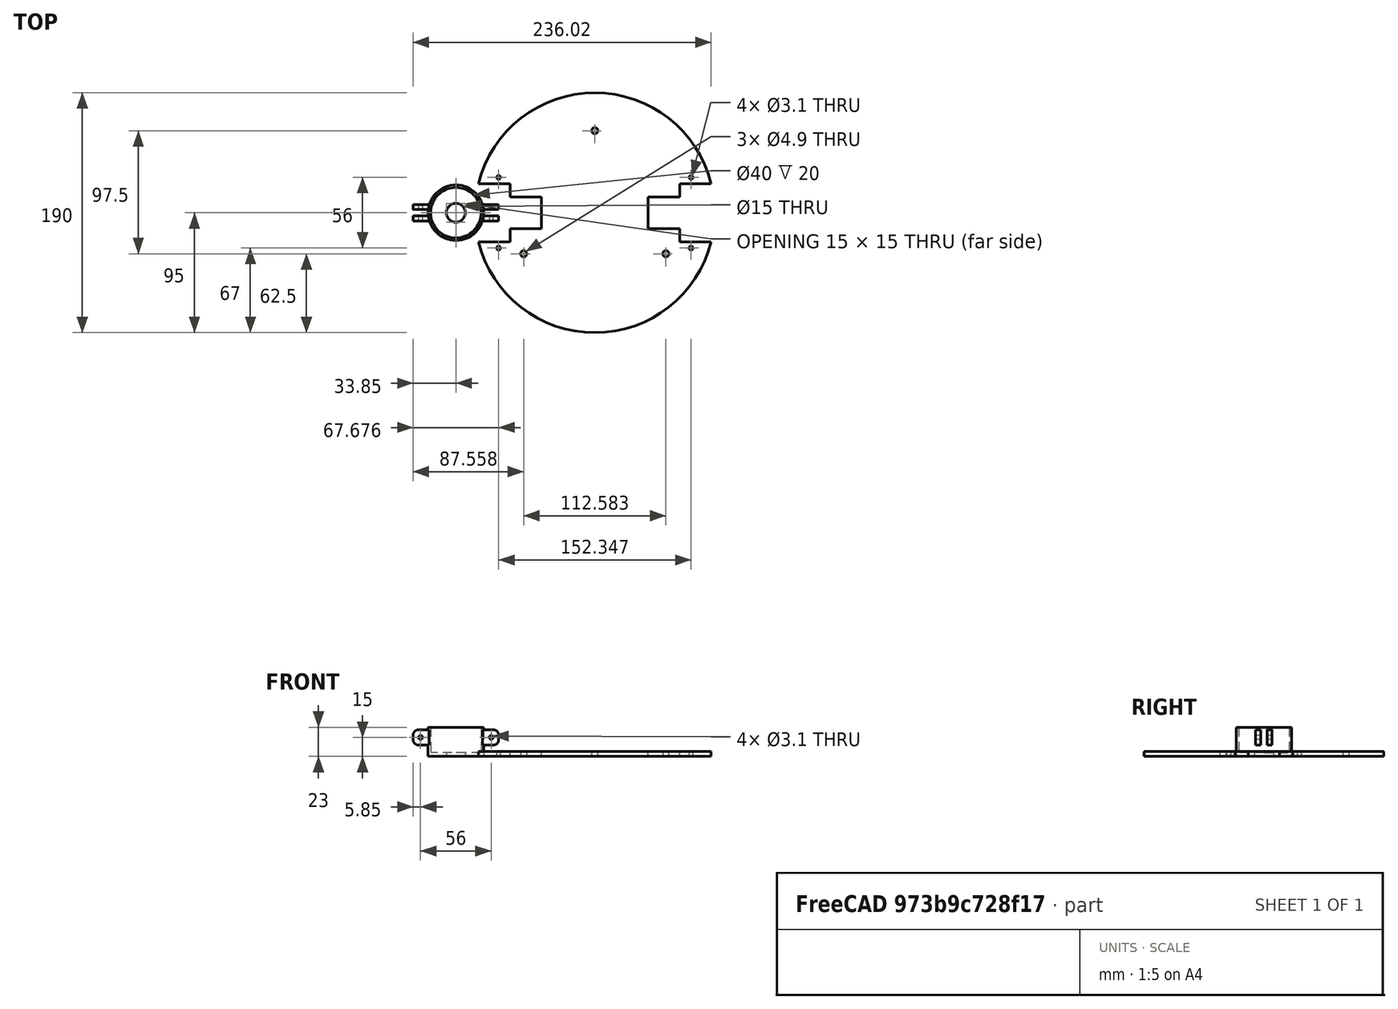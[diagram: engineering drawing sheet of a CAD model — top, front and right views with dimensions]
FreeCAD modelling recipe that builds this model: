
FCSTD DOCUMENT  (FreeCAD 1.0R39319 (Git))
Label: GyroBot
License: All rights reserved
LicenseURL: https://en.wikipedia.org/wiki/All_rights_reserved
objects: Sketcher::SketchObject×6, PartDesign::CoordinateSystem×5, PartDesign::Pad×4, App::DocumentObjectGroup×3, App::Link×3, PartDesign::Mirrored×2, PartDesign::Fillet×2, PartDesign::Body×2, PartDesign::Plane×1, PartDesign::Pocket×1, App::FeaturePython×1, App::Part×1, Mesh::Feature×1
note: 45 computed .brp shape members not serialized (recipe doc carries the construction recipe); baked Part::Feature solids carry a one-line shape summary decoded from their .brp

FEATURE [Sketcher::SketchObject] Sketch
  ArcFitTolerance = 1e-06
  AttachmentSupport = -> [XY_Plane]
  FullyConstrained = false
  MakeInternals = false
  MapMode = 5
  sketch-geometry (2):
    g0: Circle CenterX=0 CenterY=0 CenterZ=0 NormalX=0 NormalY=0 NormalZ=1 AngleXU=0 Radius=22
    g1: Circle CenterX=0 CenterY=0 CenterZ=0 NormalX=0 NormalY=0 NormalZ=1 AngleXU=0 Radius=7.5
  constraints (2):
    c: Diameter(g0) = 44
    c: Diameter(g1) = 15
FEATURE [PartDesign::Pad] Pad
  Direction = (0,0,1)
  Length = 3
  Length2 = 10
  Profile = -> Sketch
  ReferenceAxis = -> Sketch [N_Axis]
  Refine = true
  Suppressed = false
  Type = 0
FEATURE [Sketcher::SketchObject] Sketch001
  ArcFitTolerance = 1e-06
  AttachmentSupport = -> [Pad]
  FullyConstrained = true
  MakeInternals = false
  MapMode = 5
  Placement = pos=(0,0,3) rot=(0,0,1;0rad)
  sketch-geometry (2):
    g0: Circle CenterX=0 CenterY=0 CenterZ=0 NormalX=0 NormalY=0 NormalZ=1 AngleXU=0 Radius=22
    g1: Circle CenterX=0 CenterY=0 CenterZ=0 NormalX=0 NormalY=0 NormalZ=1 AngleXU=0 Radius=20
  constraints (4):
    c: Diameter(g0) = 44
    c: Coincident(g0,g-1)
    c: Diameter(g1) = 40
    c: Coincident(g1,g0)
FEATURE [PartDesign::Pad] Pad001
  BaseFeature = -> Pad
  Direction = (0,0,1)
  Length = 20
  Length2 = 10
  Profile = -> Sketch001
  ReferenceAxis = -> Sketch001 [N_Axis]
  Refine = true
  Suppressed = false
  Type = 0
  UseCustomVector = true
FEATURE [PartDesign::Plane] DatumPlane
  AttachmentOffset = pos=(0,0,2.5) rot=(0,0,1;0rad)
  AttachmentSupport = -> [Pad001]
  Length = 79.3297
  MapMode = 3
  Placement = pos=(0,-2.5,6e-16) rot=(1,0,0;1.5708rad)
  ResizeMode = 0
  Width = 61.6356
FEATURE [Sketcher::SketchObject] Sketch002
  ArcFitTolerance = 1e-06
  AttachmentSupport = -> [DatumPlane]
  ExternalGeometry = -> [Pad001]
  FullyConstrained = false
  MakeInternals = false
  MapMode = 5
  Placement = pos=(0,-2.5,6e-16) rot=(1,0,0;1.5708rad)
  sketch-geometry (4):
    g0: LineSegment StartX=20.847 StartY=20.9308 StartZ=0 EndX=20.847 EndY=8.93082 EndZ=0
    g1: LineSegment StartX=20.847 StartY=8.93082 StartZ=0 EndX=33.847 EndY=8.93082 EndZ=0
    g2: LineSegment StartX=33.847 StartY=8.93082 StartZ=0 EndX=33.847 EndY=20.9308 EndZ=0
    g3: LineSegment StartX=33.847 StartY=20.9308 StartZ=0 EndX=20.847 EndY=20.9308 EndZ=0
  constraints (10):
    c: Coincident(g0,g1)
    c: Coincident(g1,g2)
    c: Coincident(g2,g3)
    c: Coincident(g3,g0)
    c: Vertical(g0)
    c: Vertical(g2)
    c: Horizontal(g1)
    c: Horizontal(g3)
    c: Distance(g0,g2) = 13
    c: Distance(g1,g3) = 12
FEATURE [PartDesign::Pad] Pad002
  BaseFeature = -> Pad001
  Direction = (0,-1,2e-16)
  Length = 4
  Length2 = 10
  Profile = -> Sketch002
  ReferenceAxis = -> Sketch002 [N_Axis]
  Refine = true
  Suppressed = false
  Type = 0
FEATURE [PartDesign::Mirrored] Mirrored
  BaseFeature = -> Pad002
  MirrorPlane = -> XZ_Plane
  Originals = -> [Pad002]
  Refine = true
  Suppressed = false
  TransformMode = 0
FEATURE [Sketcher::SketchObject] Sketch003
  ArcFitTolerance = 1e-06
  AttachmentSupport = -> [XZ_Plane]
  FullyConstrained = true
  MakeInternals = false
  MapMode = 5
  Placement = pos=(0,0,0) rot=(1,0,0;1.5708rad)
  sketch-geometry (1):
    g0: Circle CenterX=28 CenterY=15 CenterZ=0 NormalX=0 NormalY=0 NormalZ=1 AngleXU=0 Radius=1.55
  constraints (3):
    c: Diameter(g0) = 3.1
    c: DistanceX(g-1,g0) = 28
    c: Distance(g0,g-1) = 15
FEATURE [PartDesign::Pocket] Pocket
  BaseFeature = -> Mirrored
  Direction = (0,1,-2e-16)
  Length = 30
  Length2 = 5
  Midplane = true
  Profile = -> Sketch003
  ReferenceAxis = -> Sketch003 [N_Axis]
  Refine = true
  Suppressed = false
  Type = 0
FEATURE [PartDesign::Fillet] Fillet
  Base = -> Pocket [Edge27]
  BaseFeature = -> Pocket
  Radius = 4
  Refine = true
  SupportTransform = false
  Suppressed = false
  UseAllEdges = false
FEATURE [PartDesign::Fillet] Fillet001
  Base = -> Fillet [Edge24,Edge29,Edge35]
  BaseFeature = -> Fillet
  Radius = 4
  Refine = true
  SupportTransform = false
  Suppressed = false
  UseAllEdges = false
FEATURE [PartDesign::Mirrored] Mirrored001
  BaseFeature = -> Fillet001
  MirrorPlane = -> YZ_Plane
  Originals = -> [Fillet001]
  Refine = true
  Suppressed = false
  TransformMode = 1
FEATURE [Sketcher::SketchObject] Sketch004
  ArcFitTolerance = 1e-06
  AttachmentSupport = -> [XY_Plane001]
  FullyConstrained = false
  MakeInternals = false
  MapMode = 5
  sketch-geometry (27):
    g0: ArcOfCircle CenterX=0 CenterY=0 CenterZ=0 NormalX=0 NormalY=0 NormalZ=1 AngleXU=0 Radius=95 StartAngle=0.244535 EndAngle=2.89706
    g1: Circle CenterX=0 CenterY=65 CenterZ=0 NormalX=0 NormalY=0 NormalZ=1 AngleXU=0 Radius=2.45
    g2: Circle CenterX=56.2917 CenterY=-32.5 CenterZ=0 NormalX=0 NormalY=0 NormalZ=1 AngleXU=0 Radius=2.45
    g3: LineSegment StartX=67.1737 StartY=-23 StartZ=0 EndX=92.1737 EndY=-23 EndZ=0
    g4: LineSegment StartX=92.1737 StartY=23 StartZ=0 EndX=67.1737 EndY=23 EndZ=0
    g5: LineSegment StartX=67.1737 StartY=23 StartZ=0 EndX=67.1737 EndY=12.5 EndZ=0
    g6: GeomPoint [constr] X=79.6737 Y=0 Z=0
    g7: LineSegment StartX=42.1737 StartY=-12.5 StartZ=0 EndX=67.1737 EndY=-12.5 EndZ=0
    g8: LineSegment StartX=67.1737 StartY=12.5 StartZ=0 EndX=42.1737 EndY=12.5 EndZ=0
    g9: LineSegment StartX=42.1737 StartY=12.5 StartZ=0 EndX=42.1737 EndY=-12.5 EndZ=0
    g10: GeomPoint [constr] X=54.6737 Y=0 Z=0
    g11: LineSegment StartX=67.1737 StartY=-12.5 StartZ=0 EndX=67.1737 EndY=-23 EndZ=0
    g12: Circle CenterX=76.1737 CenterY=28 CenterZ=0 NormalX=0 NormalY=0 NormalZ=1 AngleXU=0 Radius=1.55
    g13: Circle CenterX=76.1737 CenterY=-28 CenterZ=0 NormalX=0 NormalY=0 NormalZ=1 AngleXU=0 Radius=1.55
    g14: Circle CenterX=-56.2917 CenterY=-32.5 CenterZ=0 NormalX=0 NormalY=0 NormalZ=1 AngleXU=0 Radius=2.45
    g15: LineSegment StartX=-67.1737 StartY=-23 StartZ=0 EndX=-92.1737 EndY=-23 EndZ=0
    g16: LineSegment StartX=-92.1737 StartY=23 StartZ=0 EndX=-67.1737 EndY=23 EndZ=0
    g17: LineSegment StartX=-67.1737 StartY=23 StartZ=0 EndX=-67.1737 EndY=12.5 EndZ=0
    g18: GeomPoint [constr] X=-79.6737 Y=0 Z=0
    g19: LineSegment StartX=-42.1737 StartY=-12.5 StartZ=0 EndX=-67.1737 EndY=-12.5 EndZ=0
    g20: LineSegment StartX=-67.1737 StartY=12.5 StartZ=0 EndX=-42.1737 EndY=12.5 EndZ=0
    g21: LineSegment StartX=-42.1737 StartY=12.5 StartZ=0 EndX=-42.1737 EndY=-12.5 EndZ=0
    g22: GeomPoint [constr] X=-54.6737 Y=0 Z=0
    g23: LineSegment StartX=-67.1737 StartY=-12.5 StartZ=0 EndX=-67.1737 EndY=-23 EndZ=0
    g24: Circle CenterX=-76.1737 CenterY=28 CenterZ=0 NormalX=0 NormalY=0 NormalZ=1 AngleXU=0 Radius=1.55
    g25: Circle CenterX=-76.1737 CenterY=-28 CenterZ=0 NormalX=0 NormalY=0 NormalZ=1 AngleXU=0 Radius=1.55
    g26: ArcOfCircle CenterX=0 CenterY=0 CenterZ=0 NormalX=0 NormalY=0 NormalZ=1 AngleXU=0 Radius=95 StartAngle=3.38613 EndAngle=6.03865
  constraints (56):
    c: Diameter(g0) = 190
    c: Coincident(g0,g-1)
    c: Diameter(g1) = 4.9
    c: PointOnObject(g1,g-2)
    c: DistanceY(g-1,g1) = 65
    c: Diameter(g2) = 4.9
    c: Coincident(g4,g5)
    c: Coincident(g11,g3)
    c: Horizontal(g3)
    c: Horizontal(g4)
    c: Vertical(g5)
    c: Symmetric(g4,g3,g6)
    c: Distance(g3,g11) = 25
    c: Distance(g3,g4) = 46
    c: PointOnObject(g6,g-1)
    c: Coincident(g8,g9)
    c: Coincident(g9,g7)
    c: Horizontal(g7)
    c: Horizontal(g8)
    c: Vertical(g9)
    c: Symmetric(g8,g7,g10)
    c: Distance(g7,g9) = 25
    c: Distance(g7,g8) = 25
    c: PointOnObject(g10,g-1)
    c: PointOnObject(g11,g7)
    c: Diameter(g12) = 3.1
    c: DistanceY(g-1,g12) = 28
    c: Block(g5)
    c: Distance(g12,g5) = 9
    c: Diameter(g13) = 3.1
    c: Diameter(g14) = 4.9
    c: Coincident(g16,g17)
    c: Coincident(g23,g15)
    c: Horizontal(g15)
    c: Horizontal(g16)
    c: Vertical(g17)
    c: Symmetric(g16,g15,g18)
    c: Distance(g15,g23) = 25
    c: Distance(g15,g16) = 46
    c: Coincident(g20,g21)
    c: Coincident(g21,g19)
    c: Horizontal(g19)
    c: Horizontal(g20)
    c: Vertical(g21)
    c: Symmetric(g20,g19,g22)
    c: Distance(g19,g21) = 25
    c: Distance(g19,g20) = 25
    c: PointOnObject(g23,g19)
    c: Diameter(g24) = 3.1
    c: Block(g17)
    c: Distance(g24,g17) = 9
    c: Diameter(g25) = 3.1
    c: Coincident(g26,g3)
    c: Equal(g0,g26)
    c: PointOnObject(g26,g15)
    c: Coincident(g0,g26)
FEATURE [PartDesign::Pad] Pad003
  Direction = (0,0,1)
  Length = 4
  Length2 = 10
  Profile = -> Sketch004
  ReferenceAxis = -> Sketch004 [N_Axis]
  Refine = true
  Suppressed = false
  Type = 0
FEATURE [Sketcher::SketchObject] Sketch005
  ArcFitTolerance = 1e-06
  AttachmentSupport = -> [XY_Plane001]
  FullyConstrained = true
  MakeInternals = false
  MapMode = 5
FEATURE [PartDesign::CoordinateSystem] LCS_Origin
  AttacherType = Attacher::AttachEngine3D
  AttachmentSupport = -> [X_Axis002]
  MapMode = 2
FEATURE [App::DocumentObjectGroup] Constraints
FEATURE [App::FeaturePython] Variables  # WARN: FeaturePython — macro-defined, semantics opaque (R4)
  Type = App::PropertyContainer
FEATURE [App::DocumentObjectGroup] Configurations
FEATURE [PartDesign::CoordinateSystem] Base_Center
  AttacherType = Attacher::AttachEngine3D
  AttachmentSupport = -> [Pad003]
  MapMode = 5
  Placement = pos=(0,0,0) rot=(1,0,0;3.14159rad)
FEATURE [App::Link] GyroBase  label="GyroBase001"
  AttachedBy = #Base_Center
  AttachedTo = Parent Assembly#LCS_Origin
  AttachmentOffset = pos=(0,0,0) rot=(0,1,0;3.14159rad)
  LinkPlacement = pos=(0,0,0) rot=(0,0,1;3.14159rad)
  LinkedObject = -> Body001
  Placement = pos=(0,0,0) rot=(0,0,1;3.14159rad)
  SolverId = Asm4EE
  expr: Placement = LCS_Origin.Placement * AttachmentOffset * Base_Center.Placement ^ -1
FEATURE [PartDesign::CoordinateSystem] screw_hole1
  AttacherType = Attacher::AttachEngine3D
  AttachmentSupport = -> [Pad003]
  MapMode = 11
  Placement = pos=(-76.1737,-28,4) rot=(0,0,1;1.5708rad)
FEATURE [PartDesign::CoordinateSystem] screw_hole2
  AttacherType = Attacher::AttachEngine3D
  AttachmentSupport = -> [Pad003]
  MapMode = 11
  Placement = pos=(76.1737,28,4) rot=(0,0,1;1.5708rad)
FEATURE [PartDesign::Body] Body001  label="GyroBase"
  AllowCompound = false
  Group = -> [Sketch004,Pad003,Sketch005,Base_Center,screw_hole1,screw_hole2]
  Origin = -> Origin001
  Tip = -> Pad003
FEATURE [PartDesign::CoordinateSystem] motor_screw
  AttacherType = Attacher::AttachEngine3D
  AttachmentSupport = -> [Mirrored001]
  MapMode = 11
  Placement = pos=(28,-2.5,15) rot=(0.57735,-0.57735,0.57735;2.0944rad)
FEATURE [PartDesign::Body] Body  label="MotorMount"
  AllowCompound = false
  Group = -> [Sketch,Pad,Sketch001,Pad001,DatumPlane,Sketch002,Pad002,Mirrored,Sketch003,Pocket,Fillet,Fillet001,Mirrored001,motor_screw]
  Origin = -> Origin
  Placement = pos=(-110,0,0) rot=(0,0,1;0rad)
  Tip = -> Mirrored001
FEATURE [App::DocumentObjectGroup] Parts
  Group = -> [Body,Body001]
FEATURE [App::Link] MotorMount  label="MotorMount001"
  AttachedBy = #motor_screw
  AttachedTo = GyroBase#screw_hole1
  AttachmentOffset = pos=(0,0,0) rot=(0,0,1;4.71239rad)
  LinkPlacement = pos=(91.1737,-7.1e-15,1.5) rot=(0.57735,0.57735,-0.57735;4.18879rad)
  LinkedObject = -> Body
  Placement = pos=(91.1737,-7.1e-15,1.5) rot=(0.57735,0.57735,-0.57735;4.18879rad)
  SolverId = Asm4EE
  expr: Placement = GyroBase.Placement * screw_hole1.Placement * AttachmentOffset * motor_screw.Placement ^ -1
FEATURE [App::Link] MotorMount001  label="MotorMount002"
  AttachedBy = #motor_screw
  AttachedTo = GyroBase#screw_hole2
  AttachmentOffset = pos=(0,0,0) rot=(0,0,1;1.5708rad)
  LinkPlacement = pos=(-91.1737,7.1e-15,1.5) rot=(0.57735,-0.57735,0.57735;4.18879rad)
  LinkedObject = -> Body
  Placement = pos=(-91.1737,7.1e-15,1.5) rot=(0.57735,-0.57735,0.57735;4.18879rad)
  SolverId = Asm4EE
  expr: Placement = GyroBase.Placement * screw_hole2.Placement * AttachmentOffset * motor_screw.Placement ^ -1
FEATURE [App::Part] Assembly  label="GyroAssembly"
  AssemblyType = Part::Link
  Group = -> [LCS_Origin,Constraints,Variables,Configurations,GyroBase,MotorMount,MotorMount001]
  Origin = -> Origin002
  Type = Assembly
FEATURE [Mesh::Feature] GyroBot_Parts  label="GyroBot-Parts"
